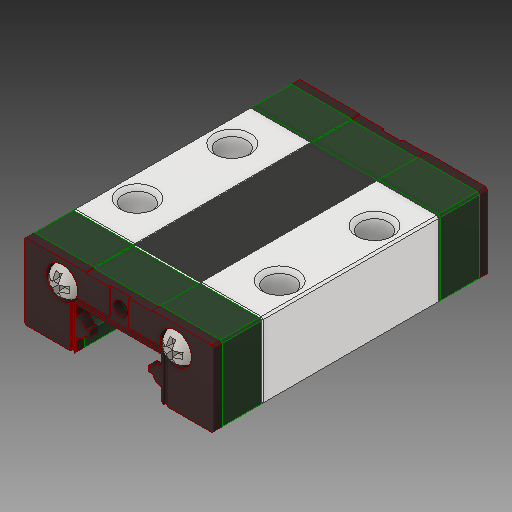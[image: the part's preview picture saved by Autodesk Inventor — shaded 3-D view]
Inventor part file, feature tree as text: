
AUTODESK INVENTOR PART (.ipt)
format: ipt  version: 2019 (Build 230136000, 136)  size: 480,768 bytes
history: mixed  units: mm
features: extrude x6, mirror x4, sketch x2, surface_op x1, direct_edit x1, plane x1, chamfer x1, move_body x1, imported_body x1
ambient origin geometry x8: Origin, YZ Plane, XZ Plane, XY Plane, X Axis, Y Axis, Z Axis, Center Point
bodies: Solid1 (imported_parasolid), Solid2 (imported_parasolid), Solid3 (imported_parasolid), Solid4 (imported_parasolid), Solid9 (imported_parasolid)
feature tree (18):
  surface_op  "Sculpt1"
  direct_edit  "Direct Edit1"
  plane  "Work Plane1"
  mirror  "Mirror1"
  mirror  "Mirror2"
  mirror  "Mirror3"
  extrude  "Extrusion1"  Depth=5.5mm
  mirror  "Mirror4"
  extrude  "Extrusion2"  Depth=5.0mm
  chamfer  "Chamfer1"  Distance=10.0mm
  sketch  "Sketch2"  dims[d0=0.0mm d1=5.5mm d2=0.0mm d3=5.5mm]
  sketch  "Sketch3"  dims[d4=3.8mm d5=5.0mm d6=10.0mm d7=0.0mm d8=14.45mm d10=10.0mm d11=15.0mm d12=3.0mm d13=4.0mm d14=0.0mm d15=0.4mm d16=2.0mm d17=45.0deg]
  extrude  "Extrude2"  Depth=0.4mm
  extrude  "Extrude6[1]"  Depth=10.0mm
  extrude  "Extrude6[2]"  Depth=0.4mm
  extrude  "Extrude7"  Depth=0.4mm
  move_body  "Move1"
  imported_body  NMx_Import_Brep_tag  [imported B-rep: ~327 faces, bbox_mm=[20.0, 8.0, 30.285311]]
